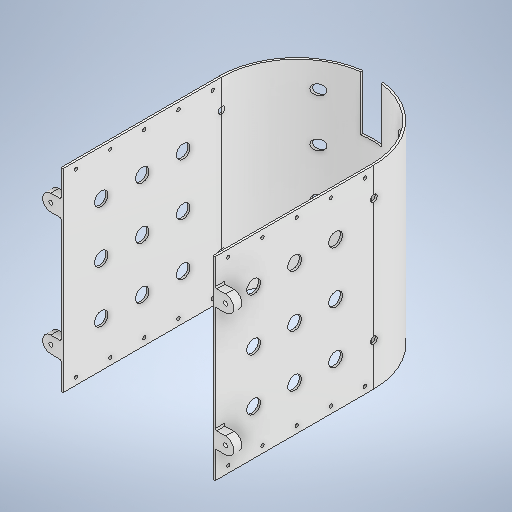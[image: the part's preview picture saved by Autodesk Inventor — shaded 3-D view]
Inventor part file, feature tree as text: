
AUTODESK INVENTOR PART (.ipt)
format: ipt  version: 2025.1 (Build 291241000, 241)  size: 463,872 bytes
history: native  units: mm
features: sketch x8, mirror x6, extrude x4, hole x4, plane x1, fillet x1, projected_geometry x1
ambient origin geometry x8: Origin, YZ Plane, XZ Plane, XY Plane, X Axis, Y Axis, Z Axis, Center Point
bodies: Volumenkörper1 (feature_tree)
feature tree (25):
  extrude  "Extrusion1"  Depth=1.5mm
  plane  "Arbeitsebene1"
  extrude  "Extrusion2"  Depth=116.0mm TaperAngle=0.0deg
  extrude  "Extrusion3"  Depth=40.0mm
  mirror  "Spiegeln1"
  hole  "Bohrung1"  [1 undecoded]
  mirror  "Spiegeln2"
  hole  "Bohrung2"  [1 undecoded]
  mirror  "Spiegeln3"
  extrude  "Extrusion4"  Depth=142.0mm TaperAngle=0.0deg
  hole  "Bohrung3"  [1 undecoded]
  fillet  "Rundung1"  Radius=18.5mm
  mirror  "Spiegeln4"
  hole  "Bohrung4"  [1 undecoded]
  mirror  "Spiegeln5"
  mirror  "Spiegeln6"
  sketch  "Skizze1"  dims[d0=1.5mm d1=110.0mm]
  sketch  "Skizze2"  dims[d2=116.0mm d3=142.0mm d4=0.0mm]
  projected_geometry  "Projizierte Kontur1"
  sketch  "Skizze3"  dims[d5=173.0mm d6=40.0mm]
  sketch  "Skizze4"  dims[d7=15.0mm d8=15.0mm]
  sketch  "Skizze5"  dims[d9=15.0mm d10=31.0mm]
  sketch  "Skizze6"  dims[d11=38.0mm d12=142.0mm d13=0.0mm]
  sketch  "Skizze7"  dims[d14=30.0mm d15=7.5mm d16=18.5mm]
  sketch  "Skizze8"  dims[d17=35.0mm d18=35.0mm d19=35.0mm d20=10.0mm d21=0.0mm d22=50.0mm d23=40.0mm d24=5.0mm d25=6.0mm d26=4.0mm d27=2.0mm d28=90.0deg d29=8.0mm d30=0.0mm d31=38.0mm d32=38.0mm d33=33.0mm d34=30.0mm d35=30.0mm d36=10.0mm d37=6.0mm d38=4.0mm d39=2.0mm d40=90.0deg d41=8.0mm d42=0.0mm d43=6.0mm d44=6.0mm d47=26.0mm d48=90.0mm d49=64.0mm d50=6.0mm d51=0.0mm d52=3.0mm d53=6.0mm d54=4.0mm d55=2.0mm d56=90.0deg d57=8.0mm d58=0.0mm d59=1.0mm d60=9.5mm d61=25.0mm d62=25.0mm d63=25.0mm d64=25.0mm d65=5.0mm d66=2.459mm d67=6.0mm d68=4.0mm d69=2.0mm d70=90.0deg d71=8.0mm d72=0.0mm]
note: 4 required parameter values undecoded (feature->parameter linkage not recoverable at this tier; creation-order binding heuristic only, values carry confidence <= 0.55)
